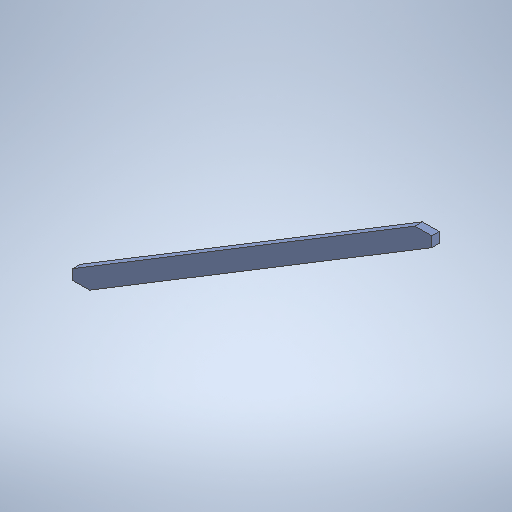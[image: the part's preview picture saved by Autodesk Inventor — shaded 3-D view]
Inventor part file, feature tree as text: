
AUTODESK INVENTOR PART (.ipt)
format: ipt  version: 2025.1 (Build 291241020, 241B)  size: 252,928 bytes
history: native  units: in
note: dims shown in document units (in); Inventor stores cm internally (conversion verified against a paired STEP export)
features: other x7, reference x4, extrude x1, sketch x1
ambient origin geometry x8: Origin, YZ Plane, XZ Plane, XY Plane, X Axis, Y Axis, Z Axis, Center Point
bodies: Solid1 (feature_tree)
feature tree (13):
  extrude  "Extrusion1"  [1 undecoded]
  sketch  "Sketch1"  dims[d2=1.5in d3=0.0in]
  reference  "Reference1"
  reference  "Reference2"
  reference  "Reference3"
  reference  "Reference4"
  other  "<userpath>\Documents\Tburn24\Assembly1.iam"
  other  "Assembly1.iam"
  other  "6'x2x4:1"
  other  "16'x4x4:1"
  other  "16'x2x4:2"
  other  "6'x4x4:18"
  other  "Finish1"
note: 1 required parameter value undecoded (feature->parameter linkage not recoverable at this tier; creation-order binding heuristic only, values carry confidence <= 0.55)
